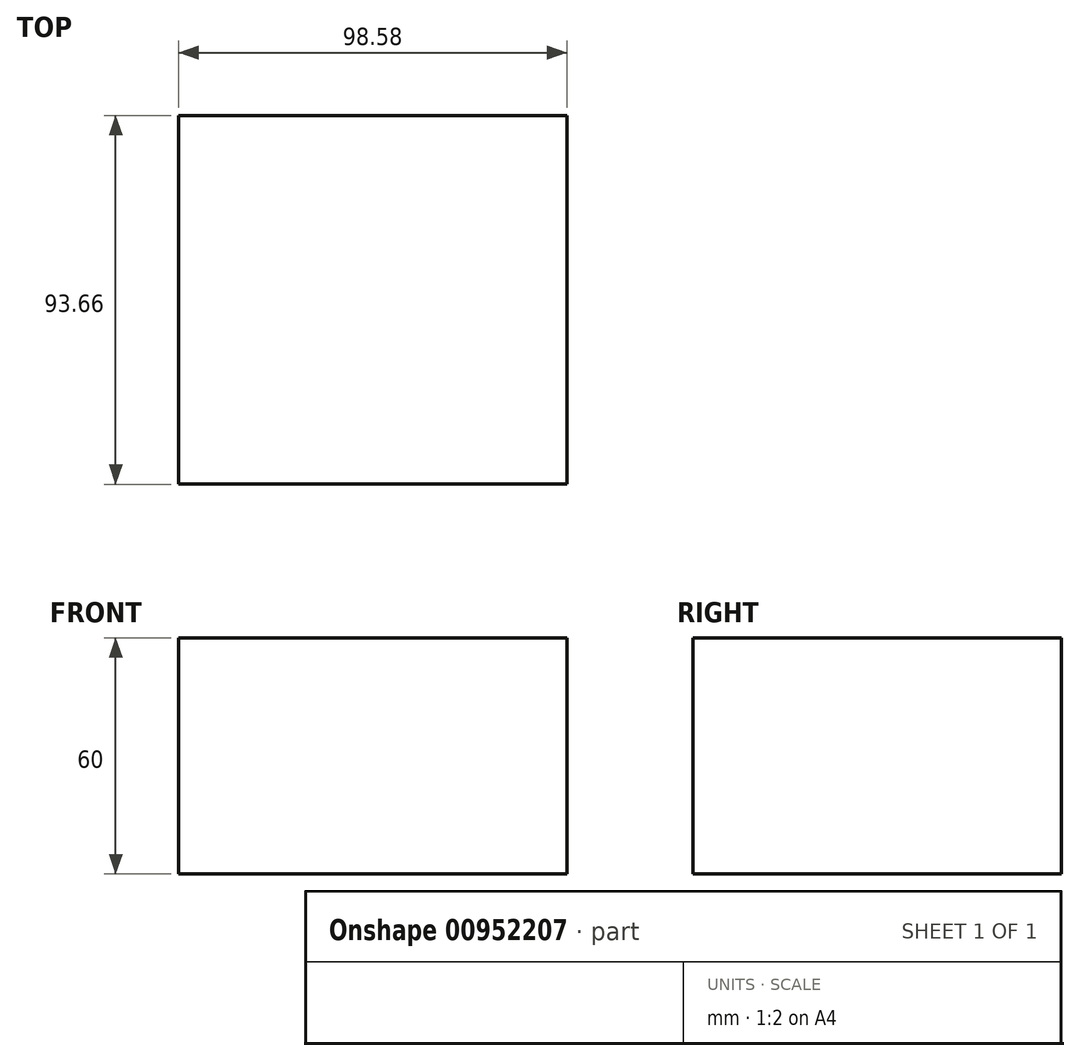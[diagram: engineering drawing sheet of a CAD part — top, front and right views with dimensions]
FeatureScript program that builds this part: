
annotation { "Feature Type Name" : "Feature", "Feature Type Description" : "" }
export const myFeature = defineFeature(function(context is Context, id is Id, definition is map)
    precondition{}
    {
        {
            var Q0;
            Q0=qCreatedBy(makeId("Top.planeOp"),FACE);
            var sketch = newSketch(context, id + "F0", { "sketchPlane" : qUnion([Q0])});
            skLineSegment(sketch, "E0.bottom", {"start": v(-39.55, 44.13) * mm, "end": v(59.03, 44.13) * mm});
            skLineSegment(sketch, "E0.top", {"start": v(-39.55, -49.53) * mm, "end": v(59.03, -49.53) * mm});
            skLineSegment(sketch, "E0.left", {"start": v(-39.55, 44.13) * mm, "end": v(-39.55, -49.53) * mm});
            skLineSegment(sketch, "E0.right", {"start": v(59.03, 44.13) * mm, "end": v(59.03, -49.53) * mm});
            skSolve(sketch);
        }
        {
            var Q0;
            Q0=makeQuery(id+"F0.imprint","IMPRINT",FACE,{"disambiguationData":[TD([[makeQuery(id+"F0.imprint","IMPRINT",EDGE,{"derivedFrom":sQuery(id+"F0.wireOp",EDGE,"E0.bottom")}),-1.0]])]});
            extrude(context, id + "F1", {"entities" : qUnion([Q0]), "depth" : 60 * mm, "offsetDistance" : 25 * mm});
        }
    });
